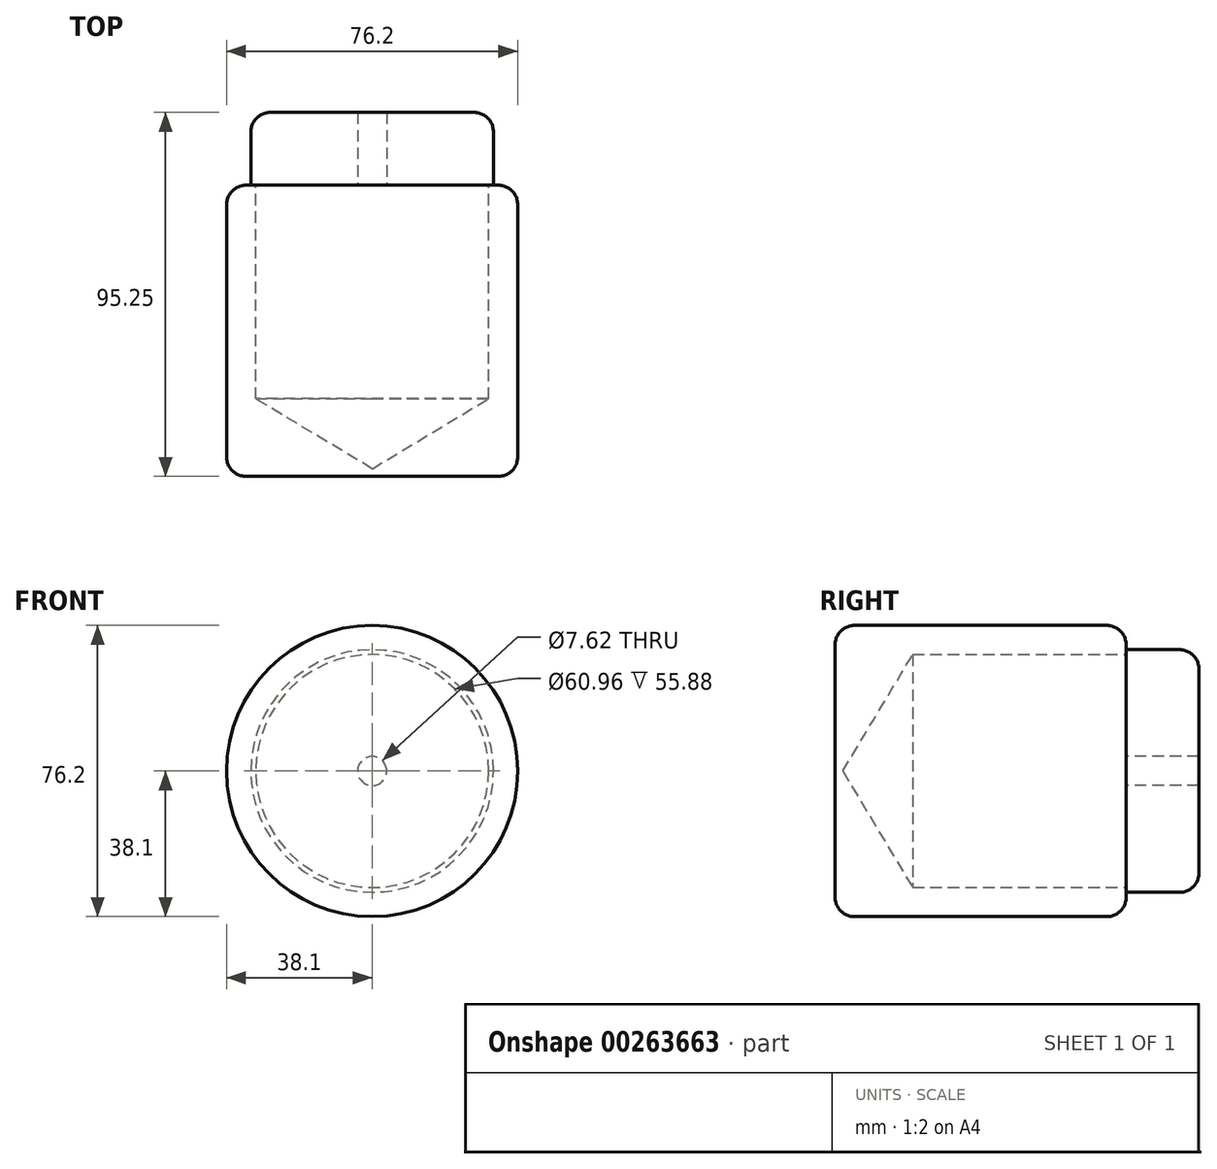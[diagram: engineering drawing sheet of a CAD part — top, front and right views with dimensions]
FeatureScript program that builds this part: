
annotation { "Feature Type Name" : "Feature", "Feature Type Description" : "" }
export const myFeature = defineFeature(function(context is Context, id is Id, definition is map)
    precondition{}
    {
        {
            var Q0;
            Q0=qCreatedBy(makeId("Front.planeOp"),FACE);
            var sketch = newSketch(context, id + "F0", { "sketchPlane" : qUnion([Q0])});
            skCircle(sketch, "E0", {"center": v(0, 0) * mm, "radius": 38.1 * mm});
            skSolve(sketch);
        }
        {
            var Q0;
            Q0=makeQuery(id+"F0.imprint","IMPRINT",FACE,{"disambiguationData":[TD([[makeQuery(id+"F0.imprint","IMPRINT",EDGE,{"derivedFrom":sQuery(id+"F0.wireOp",EDGE,"E0")}),1.0]])]});
            extrude(context, id + "F1", {"entities" : qUnion([Q0]), "depth" : 76.2 * mm});
        }
        {
            var Q0;
            Q0=qCreatedBy(makeId("Front.planeOp"),FACE);
            var sketch = newSketch(context, id + "F2", { "sketchPlane" : qUnion([Q0])});
            skCircle(sketch, "E1", {"center": v(0, 0) * mm, "radius": 31.75 * mm});
            skSolve(sketch);
        }
        {
            var Q0;
            Q0 = qSketchRegion(id + "F2", true);
            extrude(context, id + "F3", {"entities" : qUnion([Q0]), "operationType" : NewBodyOperationType.ADD, "oppositeDirection" : true, "depth" : 19.05 * mm});
        }
        {
            var Q0;
            Q0=makeQuery(id+"F3.opExtrude","CAP_EDGE",EDGE,{"disambiguationData":[OSD([sQuery(id+"F2.wireOp",EDGE,"E1")])],"isStart":false});
            var Q1;
            Q1=makeQuery(id+"F1.opExtrude","SWEPT_FACE",FACE,{"disambiguationData":[OSD([sQuery(id+"F0.wireOp",EDGE,"E0")])]});
            fillet(context, id + "F4", {"entities" : qUnion([Q0, Q1]), "radius" : 5.08 * mm, "tangentPropagation" : true, "allowEdgeOverflow" : false});
        }
        {
            var Q0;
            Q0=qCreatedBy(makeId("Front.planeOp"),FACE);
            var sketch = newSketch(context, id + "F5", { "sketchPlane" : qUnion([Q0])});
            skCircle(sketch, "E2", {"center": v(0, 0) * mm, "radius": 3.81 * mm});
            skSolve(sketch);
        }
        {
            var Q0;
            Q0=sQuery(id+"F5.wireOp",VERTEX,"E2.center");
            var Q1;
            Q1=makeQuery(id+"F1.opExtrude","SWEPT_BODY",BODY,{"disambiguationData":[OSD([sQuery(id+"F0.wireOp",EDGE,"E0")])]});
            hole(context, id + "F6", {"style" : HoleStyle.SIMPLE, "endStyle" : HoleEndStyle.BLIND, "holeDiameter" : 7.62 * mm, "holeDepth" : 21.59 * mm, "tappedDepth" : 12.7 * mm, "tapClearance" : 3, "locations" : qUnion([Q0]), "scope" : qUnion([Q1])});
        }
        {
            var Q0;
            Q0=sQuery(id+"F5.wireOp",VERTEX,"E2.center");
            var Q1;
            Q1=makeQuery(id+"F1.opExtrude","SWEPT_BODY",BODY,{"disambiguationData":[OSD([sQuery(id+"F0.wireOp",EDGE,"E0")])]});
            hole(context, id + "F7", {"style" : HoleStyle.SIMPLE, "endStyle" : HoleEndStyle.BLIND, "oppositeDirection" : true, "holeDiameter" : 60.96 * mm, "holeDepth" : 55.88 * mm, "tappedDepth" : 12.7 * mm, "tapClearance" : 3, "locations" : qUnion([Q0]), "scope" : qUnion([Q1])});
        }
    });
